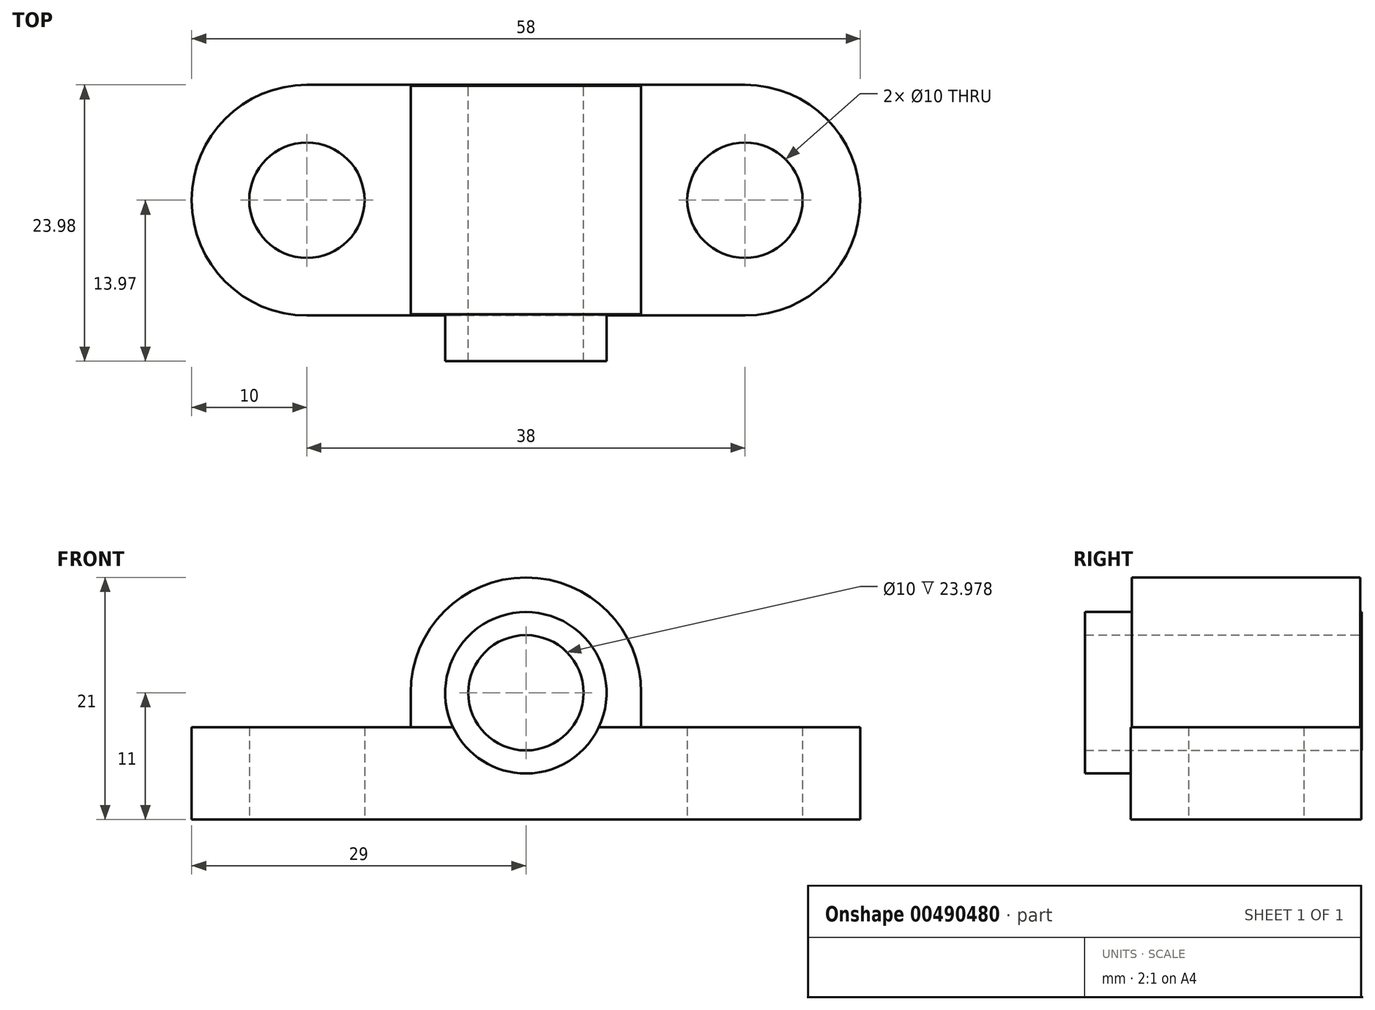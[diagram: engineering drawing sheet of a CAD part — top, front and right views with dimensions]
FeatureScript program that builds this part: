
annotation { "Feature Type Name" : "Feature", "Feature Type Description" : "" }
export const myFeature = defineFeature(function(context is Context, id is Id, definition is map)
    precondition{}
    {
        {
            var Q0;
            Q0=qCreatedBy(makeId("Top.planeOp"),FACE);
            var sketch = newSketch(context, id + "F0", { "sketchPlane" : qUnion([Q0])});
            skLineSegment(sketch, "E0", {"start": v(-42.29, 0) * mm, "end": v(44.43, 0) * mm, "construction": true});
            skLineSegment(sketch, "E1", {"start": v(0, 19.67) * mm, "end": v(0, -19.03) * mm, "construction": true});
            skLineSegment(sketch, "E2", {"start": v(-19, 18.28) * mm, "end": v(-19, -13.72) * mm, "construction": true});
            skLineSegment(sketch, "E3", {"start": v(19, 18.5) * mm, "end": v(19, -15.92) * mm, "construction": true});
            skCircle(sketch, "E4", {"center": v(-19, 0) * mm, "radius": 5 * mm});
            skCircle(sketch, "E5", {"center": v(19, 0) * mm, "radius": 5 * mm});
            skArc(sketch, "E6", {"start": v(19, -10) * mm, "mid": v(29, 0) * mm, "end": v(19, 10) * mm});
            skArc(sketch, "E7", {"start": v(-19, -10) * mm, "mid": v(-29, 0) * mm, "end": v(-19, 10) * mm});
            skLineSegment(sketch, "E8", {"start": v(-19, 10) * mm, "end": v(19, 10) * mm});
            skLineSegment(sketch, "E9", {"start": v(-19, -10) * mm, "end": v(19, -10) * mm});
            skSolve(sketch);
        }
        {
            var Q0;
            Q0 = qSketchRegion(id + "F0", true);
            extrude(context, id + "F1", {"entities" : qUnion([Q0]), "depth" : 8 * mm});
        }
        {
            var Q0;
            Q0=qCreatedBy(makeId("Front.planeOp"),FACE);
            var sketch = newSketch(context, id + "F2", { "sketchPlane" : qUnion([Q0])});
            skLineSegment(sketch, "E10", {"start": v(0, 41.3) * mm, "end": v(0, -20.8) * mm, "construction": true});
            skLineSegment(sketch, "E11", {"start": v(-46.9, 11) * mm, "end": v(59.08, 11) * mm, "construction": true});
            skArc(sketch, "E12", {"start": v(10, 11) * mm, "mid": v(0, 21) * mm, "end": v(-10, 11) * mm});
            skLineSegment(sketch, "E13", {"start": v(10, 11) * mm, "end": v(10, 0) * mm});
            skLineSegment(sketch, "E14", {"start": v(-10, 11) * mm, "end": v(-10, 0) * mm});
            skLineSegment(sketch, "E15", {"start": v(-10, 0) * mm, "end": v(10, 0) * mm});
            skSolve(sketch);
        }
        {
            var Q0;
            Q0 = qSketchRegion(id + "F2", true);
            extrude(context, id + "F3", {"entities" : qUnion([Q0]), "operationType" : NewBodyOperationType.ADD, "endBound" : BoundingType.SYMMETRIC, "depth" : 19.8 * mm});
        }
        {
            var Q0;
            Q0=qCreatedBy(makeId("Front.planeOp"),FACE);
            var sketch = newSketch(context, id + "F4", { "sketchPlane" : qUnion([Q0])});
            skLineSegment(sketch, "E16", {"start": v(-45.98, 11) * mm, "end": v(52.9, 11) * mm, "construction": true});
            skLineSegment(sketch, "E17", {"start": v(0, 31.32) * mm, "end": v(0, -9.8) * mm, "construction": true});
            skCircle(sketch, "E18", {"center": v(0, 11) * mm, "radius": 7 * mm});
            skSolve(sketch);
        }
        {
            var Q0;
            Q0 = qSketchRegion(id + "F4", true);
            extrude(context, id + "F5", {"entities" : qUnion([Q0]), "operationType" : NewBodyOperationType.REMOVE, "endBound" : BoundingType.THROUGH_ALL, "depth" : 25.4 * mm, "hasSecondDirection" : true, "secondDirectionBound" : SecondDirectionBoundingType.THROUGH_ALL, "secondDirectionOppositeDirection" : true, "secondDirectionDepth" : 25.4 * mm});
        }
        {
            var Q0;
            Q0=qCreatedBy(makeId("Front.planeOp"),FACE);
            var sketch = newSketch(context, id + "F6", { "sketchPlane" : qUnion([Q0])});
            skLineSegment(sketch, "E19", {"start": v(0, 29) * mm, "end": v(0, -16.25) * mm, "construction": true});
            skLineSegment(sketch, "E20", {"start": v(-38.86, 11) * mm, "end": v(38.25, 11) * mm, "construction": true});
            skCircle(sketch, "E21", {"center": v(0, 11) * mm, "radius": 7 * mm});
            skCircle(sketch, "E22", {"center": v(0, 11) * mm, "radius": 5 * mm});
            skSolve(sketch);
        }
        {
            var Q0;
            Q0 = qSketchRegion(id + "F6", true);
            extrude(context, id + "F7", {"entities" : qUnion([Q0]), "operationType" : NewBodyOperationType.ADD, "depth" : 13.97 * mm, "hasSecondDirection" : true, "secondDirectionOppositeDirection" : true, "secondDirectionDepth" : 10 * mm});
        }
    });
